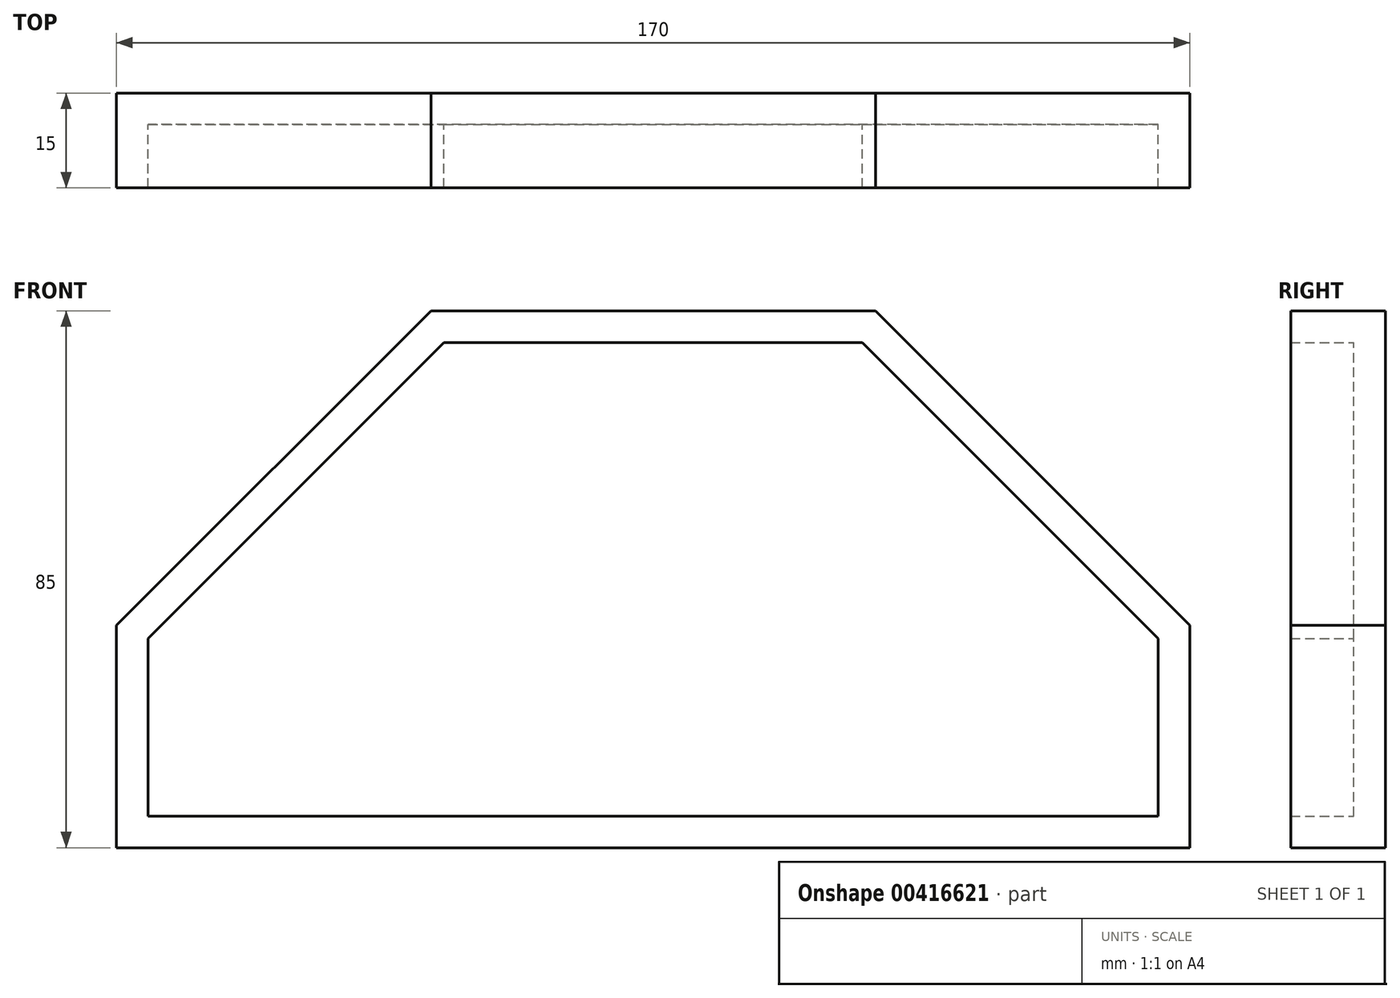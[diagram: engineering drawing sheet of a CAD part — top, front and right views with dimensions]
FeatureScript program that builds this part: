
annotation { "Feature Type Name" : "Feature", "Feature Type Description" : "" }
export const myFeature = defineFeature(function(context is Context, id is Id, definition is map)
    precondition{}
    {
        {
            var Q0;
            Q0=qCreatedBy(makeId("Front.planeOp"),FACE);
            var sketch = newSketch(context, id + "F0", { "sketchPlane" : qUnion([Q0])});
            skCircle(sketch, "E0.cCircle", {"center": v(0, 0) * mm, "radius": 85 * mm, "construction": true});
            skLineSegment(sketch, "E0.0", {"start": v(85, 35.2) * mm, "end": v(85, 0) * mm});
            skLineSegment(sketch, "E0.4", {"start": v(-85, 0) * mm, "end": v(-85, 35.2) * mm});
            skLineSegment(sketch, "E0.5", {"start": v(-85, 35.2) * mm, "end": v(-35.2, 85) * mm});
            skLineSegment(sketch, "E0.6", {"start": v(-35.2, 85) * mm, "end": v(35.2, 85) * mm});
            skLineSegment(sketch, "E0.7", {"start": v(35.2, 85) * mm, "end": v(85, 35.2) * mm});
            skPoint(sketch, "E0.0.midPoint", {"position": v(85, 0) * mm});
            skLineSegment(sketch, "E1", {"start": v(85, 0) * mm, "end": v(-85, 0) * mm});
            skPoint(sketch, "E2.orphan", {"position": v(-85, -35.2) * mm});
            skPoint(sketch, "E3.orphan", {"position": v(85, -35.2) * mm});
            skPoint(sketch, "E4.orphan", {"position": v(35.2, -85) * mm});
            skSolve(sketch);
        }
        {
            var Q0;
            Q0=makeQuery(id+"F0.imprint","IMPRINT",FACE,{"disambiguationData":[TD([[makeQuery(id+"F0.imprint","IMPRINT",EDGE,{"derivedFrom":sQuery(id+"F0.wireOp",EDGE,"E0.0")}),-1.0]])]});
            extrude(context, id + "F1", {"entities" : qUnion([Q0]), "depth" : 15 * mm});
        }
        {
            var Q0;
            Q0=makeQuery(id+"F1.opExtrude","CAP_FACE",FACE,{"disambiguationData":[OSD([sQuery(id+"F0.wireOp",EDGE,"E0.0"),sQuery(id+"F0.wireOp",EDGE,"E0.4"),sQuery(id+"F0.wireOp",EDGE,"E0.5"),sQuery(id+"F0.wireOp",EDGE,"E0.6"),sQuery(id+"F0.wireOp",EDGE,"E0.7"),sQuery(id+"F0.wireOp",EDGE,"E1")])],"isStart":false});
            shell(context, id + "F2", {"entities" : qUnion([Q0]), "thickness" : 5 * mm});
        }
    });
